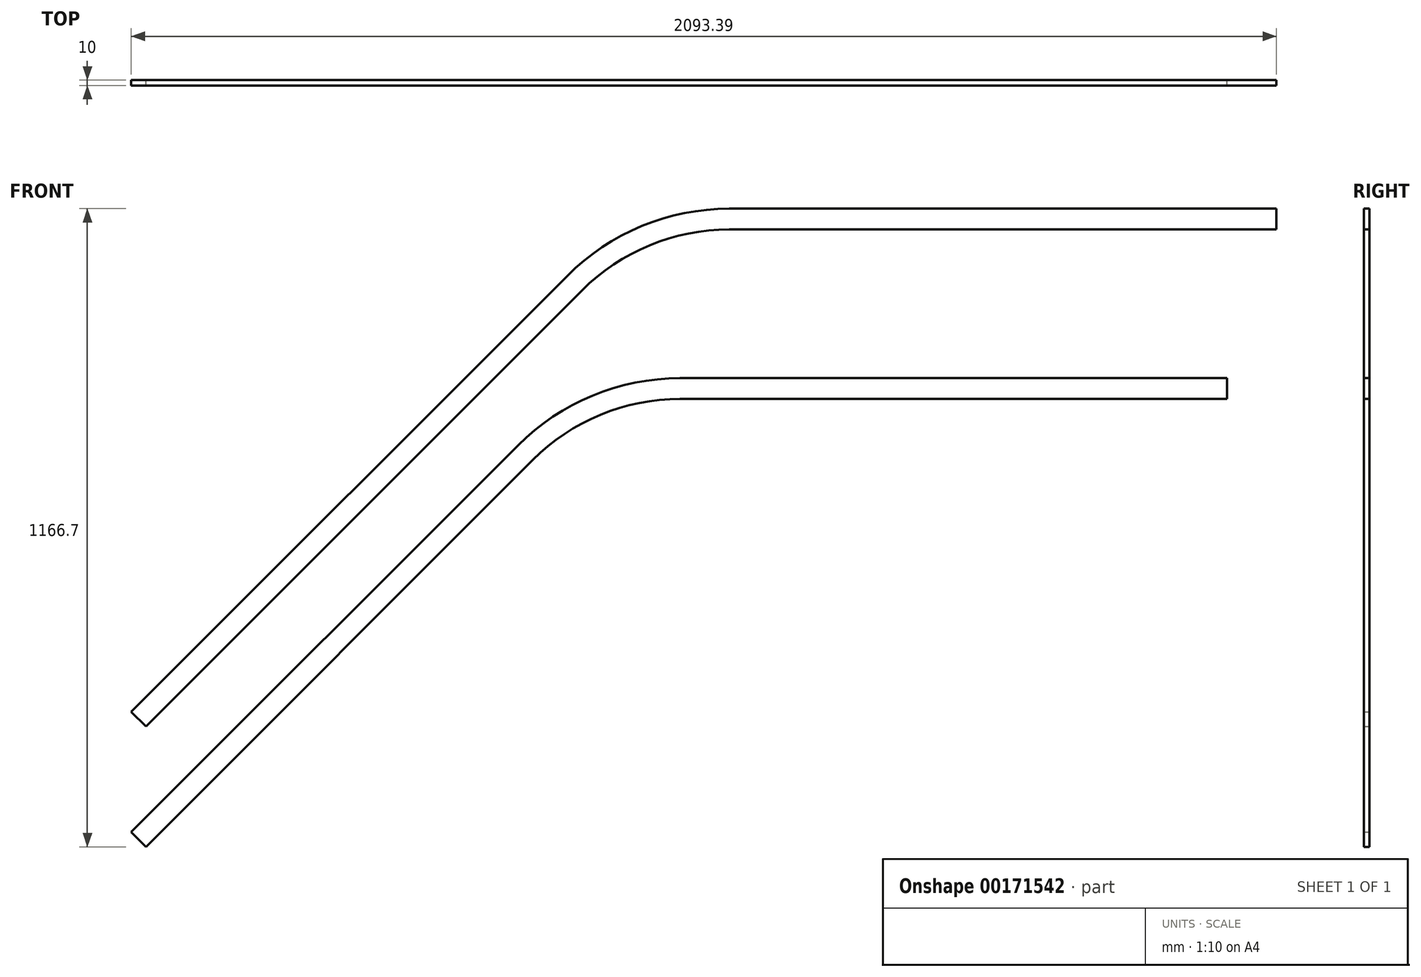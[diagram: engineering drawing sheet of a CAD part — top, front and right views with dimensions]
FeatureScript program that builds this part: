
annotation { "Feature Type Name" : "Feature", "Feature Type Description" : "" }
export const myFeature = defineFeature(function(context is Context, id is Id, definition is map)
    precondition{}
    {
        {
            var Q0;
            Q0=qCreatedBy(makeId("Front.planeOp"),FACE);
            var sketch = newSketch(context, id + "F0", { "sketchPlane" : qUnion([Q0])});
            skLineSegment(sketch, "E0", {"start": v(0, 0) * mm, "end": v(707.1, 707.1) * mm, "construction": true});
            skLineSegment(sketch, "E1", {"start": v(0, 0) * mm, "end": v(0, 220) * mm, "construction": true});
            skLineSegment(sketch, "E2", {"start": v(0, 220) * mm, "end": v(707.1, 927.1) * mm, "construction": true});
            skLineSegment(sketch, "E3", {"start": v(707.1, 927.1) * mm, "end": v(707.1, 707.1) * mm, "construction": true});
            skLineSegment(sketch, "E4", {"start": v(707.1, 927.1) * mm, "end": v(693.67, 940.54) * mm});
            skLineSegment(sketch, "E5", {"start": v(0, 220) * mm, "end": v(-13.44, 233.44) * mm});
            skLineSegment(sketch, "E6", {"start": v(-13.44, 233.44) * mm, "end": v(783.67, 1030.54) * mm});
            skLineSegment(sketch, "E7", {"start": v(786.15, 1028.07) * mm, "end": v(-10.96, 230.96) * mm});
            skLineSegment(sketch, "E8", {"start": v(0, 0) * mm, "end": v(-13.44, 13.44) * mm});
            skLineSegment(sketch, "E9", {"start": v(707.1, 707.1) * mm, "end": v(693.67, 720.54) * mm});
            skLineSegment(sketch, "E10", {"start": v(693.67, 720.54) * mm, "end": v(-13.44, 13.44) * mm});
            skPoint(sketch, "E11", {"position": v(-10.96, 10.96) * mm});
            skPoint(sketch, "E12", {"position": v(696.15, 718.07) * mm});
            skLineSegment(sketch, "E13", {"start": v(696.15, 718.07) * mm, "end": v(-10.96, 10.96) * mm});
            skLineSegment(sketch, "E14", {"start": v(0, 0) * mm, "end": v(707.1, 0) * mm, "construction": true});
            skArc(sketch, "E15", {"start": v(989.95, 824.26) * mm, "mid": v(836.88, 793.82) * mm, "end": v(707.1, 707.1) * mm, "construction": true});
            skLineSegment(sketch, "E16", {"start": v(989.95, 824.26) * mm, "end": v(1989.95, 824.26) * mm, "construction": true});
            skLineSegment(sketch, "E17", {"start": v(707.1, 927.1) * mm, "end": v(797.1, 1017.1) * mm, "construction": true});
            skArc(sketch, "E18", {"start": v(1079.95, 1134.26) * mm, "mid": v(926.88, 1103.82) * mm, "end": v(797.1, 1017.1) * mm, "construction": true});
            skLineSegment(sketch, "E19", {"start": v(1079.95, 1134.26) * mm, "end": v(2079.95, 1134.26) * mm, "construction": true});
            skArc(sketch, "E20.trimOffspring", {"start": v(680.83, 707.7) * mm, "mid": v(681.84, 695.44) * mm, "end": v(683.22, 683.22) * mm, "construction": true});
            skLineSegment(sketch, "E21", {"start": v(797.1, 1017.1) * mm, "end": v(783.67, 1030.54) * mm});
            skArc(sketch, "E22.0", {"start": v(1079.95, 1153.26) * mm, "mid": v(919.6, 1121.37) * mm, "end": v(783.67, 1030.54) * mm});
            skArc(sketch, "E23.0", {"start": v(1079.94, 1149.76) * mm, "mid": v(920.94, 1118.13) * mm, "end": v(786.15, 1028.07) * mm});
            skLineSegment(sketch, "E24", {"start": v(1079.94, 1153.26) * mm, "end": v(2079.95, 1153.26) * mm});
            skLineSegment(sketch, "E25", {"start": v(1079.95, 1153.26) * mm, "end": v(2079.95, 1153.26) * mm});
            skLineSegment(sketch, "E26", {"start": v(2079.95, 1153.26) * mm, "end": v(2079.95, 1134.26) * mm});
            skArc(sketch, "E27.0", {"start": v(989.95, 843.26) * mm, "mid": v(829.6, 811.37) * mm, "end": v(693.67, 720.54) * mm});
            skArc(sketch, "E28.0", {"start": v(989.95, 839.76) * mm, "mid": v(830.94, 808.14) * mm, "end": v(696.15, 718.07) * mm});
            skLineSegment(sketch, "E29", {"start": v(989.95, 843.26) * mm, "end": v(989.95, 824.26) * mm});
            skLineSegment(sketch, "E30", {"start": v(989.95, 839.76) * mm, "end": v(1989.95, 839.76) * mm});
            skLineSegment(sketch, "E31", {"start": v(989.95, 843.26) * mm, "end": v(1989.95, 843.26) * mm});
            skLineSegment(sketch, "E32", {"start": v(1989.95, 843.26) * mm, "end": v(1989.95, 824.26) * mm});
            skLineSegment(sketch, "E33.MirrorCS", {"start": v(0, 220) * mm, "end": v(13.44, 206.56) * mm});
            skLineSegment(sketch, "E34.MirrorCS", {"start": v(13.44, 206.56) * mm, "end": v(810.54, 1003.67) * mm});
            skLineSegment(sketch, "E35.MirrorCS", {"start": v(1079.95, 1115.26) * mm, "end": v(2079.95, 1115.26) * mm});
            skLineSegment(sketch, "E36.MirrorCS", {"start": v(2079.95, 1115.26) * mm, "end": v(2079.95, 1134.26) * mm});
            skLineSegment(sketch, "E37.MirrorCS", {"start": v(1989.95, 805.26) * mm, "end": v(1989.95, 824.26) * mm});
            skLineSegment(sketch, "E38.MirrorCS", {"start": v(989.95, 805.26) * mm, "end": v(1989.95, 805.26) * mm});
            skLineSegment(sketch, "E39.MirrorCS", {"start": v(0, 0) * mm, "end": v(13.44, -13.44) * mm});
            skLineSegment(sketch, "E40.MirrorCS", {"start": v(720.54, 693.67) * mm, "end": v(13.44, -13.44) * mm});
            skArc(sketch, "E41.0", {"start": v(1079.95, 1115.26) * mm, "mid": v(934.15, 1086.26) * mm, "end": v(810.54, 1003.67) * mm});
            skArc(sketch, "E42.0", {"start": v(989.95, 805.26) * mm, "mid": v(844.15, 776.26) * mm, "end": v(720.54, 693.67) * mm});
            skLineSegment(sketch, "E43", {"start": v(1079.94, 1149.76) * mm, "end": v(2079.95, 1149.76) * mm});
            skSolve(sketch);
        }
        {
            var Q0;
            {var subQ7=sQuery(id+"F0.wireOp",EDGE,"E23.0");Q0=makeQuery(id+"F0.imprint","IMPRINT",FACE,{"disambiguationData":[TD([[makeQuery(id+"F0.imprint","IMPRINT",EDGE,{"derivedFrom":subQ7}),1.0]])]});}
            var Q1;
            {var subQ2=sQuery(id+"F0.wireOp",EDGE,"E13");Q1=makeQuery(id+"F0.imprint","IMPRINT",FACE,{"disambiguationData":[TD([[makeQuery(id+"F0.imprint","IMPRINT",EDGE,{"derivedFrom":subQ2}),1.0]])]});}
            var Q2;
            {var subQ0=sQuery(id+"F0.wireOp",EDGE,"E10");Q2=makeQuery(id+"F0.imprint","IMPRINT",FACE,{"disambiguationData":[TD([[makeQuery(id+"F0.imprint","IMPRINT",EDGE,{"derivedFrom":subQ0}),1.0]])]});}
            var Q3;
            {var subQ0=sQuery(id+"F0.wireOp",EDGE,"E6");var subQ1=sQuery(id+"F0.wireOp",EDGE,"E4");var subQ2=makeQuery(id+"F0.imprint","INTERSECT",VERTEX,{"derivedFrom":[subQ1,subQ0]});Q3=makeQuery(id+"F0.imprint","IMPRINT",FACE,{"disambiguationData":[TD([[makeQuery(id+"F0.imprint","IMPRINT",EDGE,{"disambiguationData":[TD([[subQ2,1.0]])],"derivedFrom":subQ1}),1.0]])]});}
            var Q4;
            {var subQ1=sQuery(id+"F0.wireOp",EDGE,"E22.0");Q4=makeQuery(id+"F0.imprint","IMPRINT",FACE,{"disambiguationData":[TD([[makeQuery(id+"F0.imprint","IMPRINT",EDGE,{"derivedFrom":subQ1}),1.0]])]});}
            var Q5;
            {var subQ2=sQuery(id+"F0.wireOp",EDGE,"E30");Q5=makeQuery(id+"F0.imprint","IMPRINT",FACE,{"disambiguationData":[TD([[makeQuery(id+"F0.imprint","IMPRINT",EDGE,{"derivedFrom":subQ2}),1.0]])]});}
            var Q6;
            {var subQ0=sQuery(id+"F0.wireOp",EDGE,"E27.0");Q6=makeQuery(id+"F0.imprint","IMPRINT",FACE,{"disambiguationData":[TD([[makeQuery(id+"F0.imprint","IMPRINT",EDGE,{"derivedFrom":subQ0}),1.0]])]});}
            var Q7;
            {var subQ0=sQuery(id+"F0.wireOp",EDGE,"E6");var subQ1=sQuery(id+"F0.wireOp",EDGE,"E4");var subQ2=makeQuery(id+"F0.imprint","INTERSECT",VERTEX,{"derivedFrom":[subQ1,subQ0]});Q7=makeQuery(id+"F0.imprint","IMPRINT",FACE,{"disambiguationData":[TD([[makeQuery(id+"F0.imprint","IMPRINT",EDGE,{"disambiguationData":[TD([[subQ2,1.0]])],"derivedFrom":subQ1}),-1.0]])]});}
            extrude(context, id + "F1", {"entities" : qUnion([Q0, Q1, Q2, Q3, Q4, Q5, Q6, Q7]), "depth" : 10 * mm});
        }
    });
